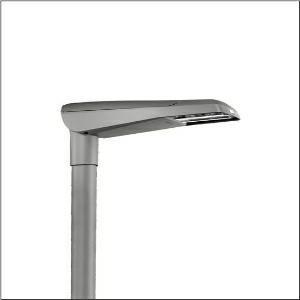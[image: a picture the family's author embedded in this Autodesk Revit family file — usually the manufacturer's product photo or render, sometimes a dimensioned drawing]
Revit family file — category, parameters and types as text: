
# Revit family: streetlight_sl_11_iq_micro___st0_5a_5xc1bc1f08de_0799
name_source: partatom
category: Lighting Fixtures
units: mm (PartAtom-declared; Revit-internal decimal feet)

## family parameters
Cut with Voids When Loaded = No
Host = Face
Light Source = No
Part Type = Normal
Room Calculation Point = No
Round Connector Dimension = Use Diameter
Shared = No

## types (1)
- --- (1 x LED, 3820 lm, 27.4 W, 4000K)
    Apparent Load = 27 VA
    CIE Flux Codes = 42 72 97 100 100
    Color Rendering = 70
    Color Temperature = 4000K
    Default Elevation = 1800 mm
    Description = Streetlight SL 11 iQ micro, mast luminaire, primary light control with 3 zone facetted reflector, of plastic, silver coated, highly specular, primary optical cover: cover, of PMMA, transparent, light distribution: ST0.5a, light emission: direct distribution, primary light characteristic: asymmetric, installation type: post-top, side-entry, lamps: LED, High Power LED, rated values: 3.590lm | 27,7W | 129,6lm/W (begin service life); end service life: 3.590lm | 28,1W; at 50% lumin. flux: 1.795lm | 13,4W | 134lm/W, colour temperature: 2200/2700/3000/4000K, colour rendering: CRI > 70, light colour: 722/727/730/740, light setting 1 begin service life: 100% | 3.590lm | 27,7W | 129,6lm/W | 3.000K, light setting 1 end service life: 28,1W, further light settings possible, control: Street-Remote, Auto-Match, Temp-Guard, Lumen-Switch, Night-Set, Smart-Wire, Light-Fading, Desk-Remote (wireless, voltage-free reading and setting of iQ features in the workshop via application-optimized NFC function/RFID function), optimised constant luminous flux control (CLO 2.0), with cable H07RN-F 5x 1.5mm², mains connection: 220..240V, AC, 50/60Hz, connection cable pre-assembled, cable length: 6,5m, luminaire housing, of diecast aluminium, powder-coated, Siteco® metallic grey (DB 702S), please order mast flange separately, inclination adjustable without tools: 0°, 5°, 10°, 15° (post-top) | 0°, -5°, -10°, -15° (side-entry), sealing non-destructively replaceable, multi-level sealing system, length: 600mm, width: 174mm, height: 116mm, mast flange for spigot size: 42mm (side-entry): 5XC10008XM4, 60/48mm (side-entry/post-top): 5XC10108XM2, 76/60mm (side-entry/post-top): 5XC10108XM1, equipment: Power, protection rating (complete): IP66, insulation class (complete): insulation class II (safety insulation), certification: CE, ENEC, ENEC+, VDE, impact resistance: IK10, permissible operating ambient temperature for outdoor applications: -25..+50°C, standard-compliant lighting for roads and squares, Environmental Product Declaration (EPD) tested and certified by an independent institute, packaging unit: 1 piece

Light Distribution: ST0.5a
    Height = 116 mm
    Lamp = 1 x LED
    Lamp Light Flux = 3820 lm
    Lamp Power = 27.4 W
    Lamp count = 1
    Length = 600 mm
    Luminous efficacy = 139 lm/W
    Manufacturer = Siteco
    ModVariant = No
    Model = 5XC1BC1F08DE
    Number of Poles = 1
    OnlyDefault = Yes
    Power Factor = 1
    Product Name = Streetlight SL 11 iQ micro | ST0.5a
    Product group = mast luminaire | pylon top
    ProductGroupID = 6100
    Protection Class = Protection class II
    Protection Degree = IP 66
    RLX_Detail_Level = 1
    RLX_Emergency_Light_Flux = 0 lm
    RLX_Emergency_Type = 0
    RLX_Emergency_Type_DB = No
    RlxData = <blob elided: 59513 chars, md5=3a4dd21a>
    Socket = socket
    Standby Power = 0 W
    System Light Flux = 3820 lm
    System Power = 27 W
    Type Comments = individual setting: luminous flux: 100 % | dim-lin: 254 | 726 mA
    Type Image = l_1006566.jpg
    URL = http://relux.com
    VarID = @adj_041570
    Voltage = 0 V
    Weight = 0.00 kg
    Width = 174 mm

## geometry (parser evidence)
native form markers: Blend x4, Sweep x10
no freeform markers — native parametric forms only
